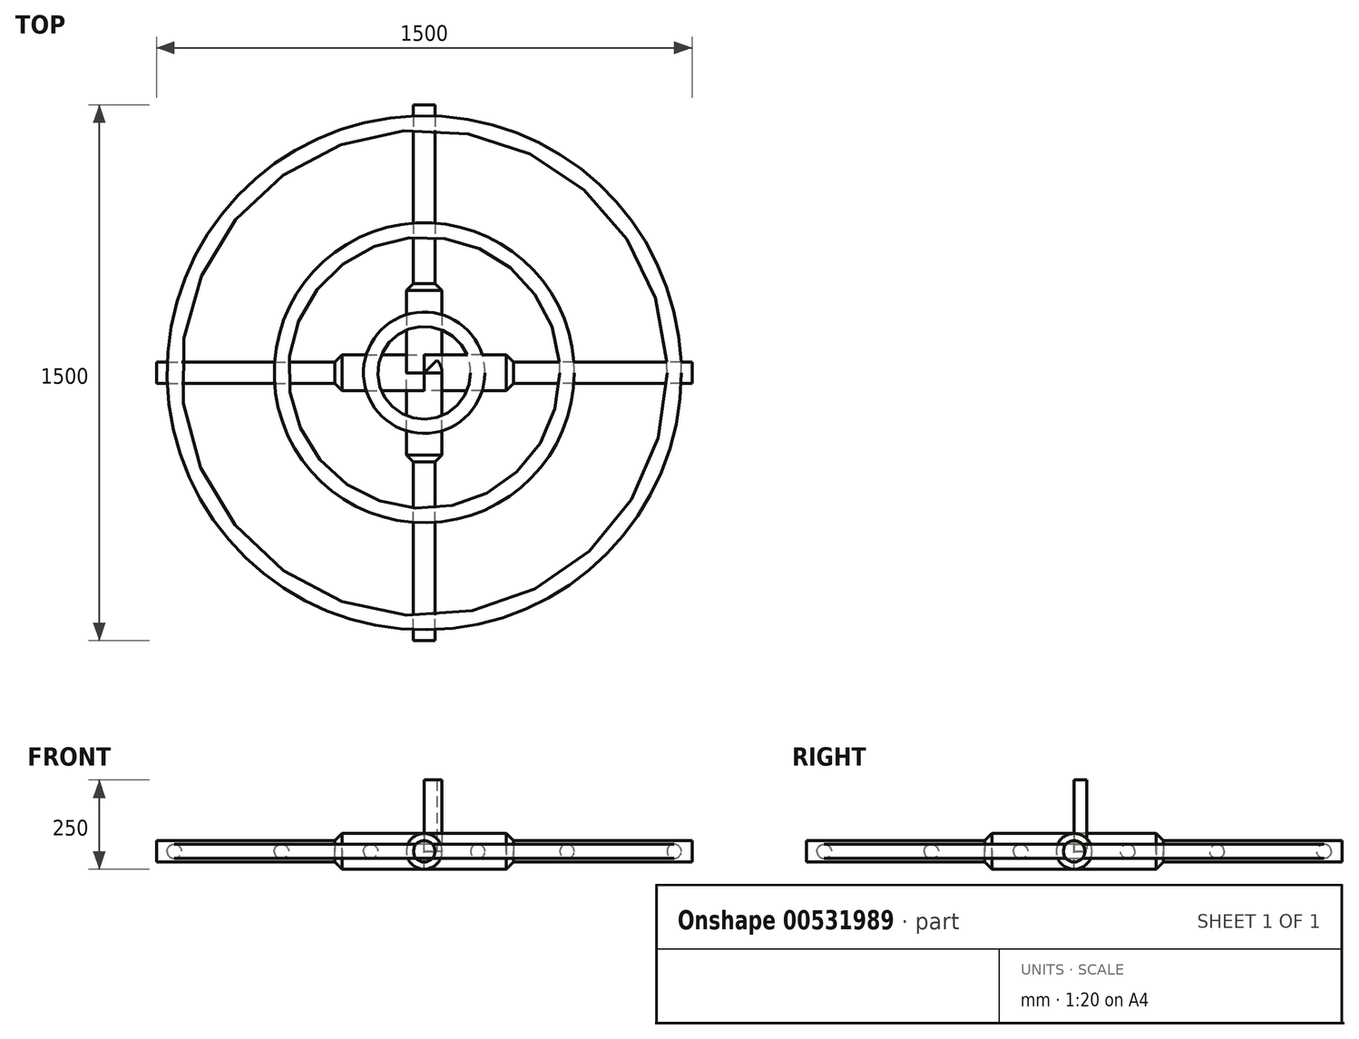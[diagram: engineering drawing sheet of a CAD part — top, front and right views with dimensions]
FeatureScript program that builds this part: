
annotation { "Feature Type Name" : "Feature", "Feature Type Description" : "" }
export const myFeature = defineFeature(function(context is Context, id is Id, definition is map)
    precondition{}
    {
        {
            var Q0;
            Q0=qCreatedBy(makeId("Top.planeOp"),FACE);
            var sketch = newSketch(context, id + "F0", { "sketchPlane" : qUnion([Q0])});
            skCircle(sketch, "E0", {"center": v(0, 0) * mm, "radius": 50 * mm});
            skSolve(sketch);
        }
        {
            var Q0;
            Q0=makeQuery(id+"F0.imprint","IMPRINT",FACE,{"disambiguationData":[TD([[makeQuery(id+"F0.imprint","IMPRINT",EDGE,{"derivedFrom":sQuery(id+"F0.wireOp",EDGE,"E0")}),1.0]])]});
            extrude(context, id + "F1", {"entities" : qUnion([Q0]), "depth" : 200 * mm, "offsetDistance" : 25 * mm});
        }
        {
            var Q0;
            Q0=qCreatedBy(makeId("Front.planeOp"),FACE);
            var sketch = newSketch(context, id + "F2", { "sketchPlane" : qUnion([Q0])});
            skCircle(sketch, "E1", {"center": v(0, 0) * mm, "radius": 50 * mm});
            skSolve(sketch);
        }
        {
            var Q0;
            Q0 = qSketchRegion(id + "F2", true);
            extrude(context, id + "F3", {"entities" : qUnion([Q0]), "depth" : 250 * mm, "offsetDistance" : 25 * mm});
        }
        {
            var Q0;
            Q0=makeQuery(id+"F3.opExtrude","CAP_FACE",FACE,{"disambiguationData":[OSD([sQuery(id+"F2.wireOp",EDGE,"E1")])],"isStart":false});
            var sketch = newSketch(context, id + "F4", { "sketchPlane" : qUnion([Q0])});
            skCircle(sketch, "E2", {"center": v(0, 0) * mm, "radius": 30 * mm});
            skSolve(sketch);
        }
        {
            var Q0;
            Q0=makeQuery(id+"F4.imprint","IMPRINT",FACE,{"disambiguationData":[TD([[makeQuery(id+"F4.imprint","IMPRINT",EDGE,{"derivedFrom":sQuery(id+"F4.wireOp",EDGE,"E2")}),1.0]])]});
            extrude(context, id + "F5", {"entities" : qUnion([Q0]), "operationType" : NewBodyOperationType.ADD, "depth" : 500 * mm, "offsetDistance" : 25 * mm});
        }
        {
            var Q0;
            Q0=makeQuery(id+"F3.opExtrude","CAP_EDGE",EDGE,{"disambiguationData":[OSD([sQuery(id+"F2.wireOp",EDGE,"E1")])],"isStart":false});
            chamfer(context, id + "F6", {"entities" : qUnion([Q0]), "width" : 20 * mm, "tangentPropagation" : true});
        }
        {
            var Q0;
            Q0=qCreatedBy(makeId("Right.planeOp"),FACE);
            var sketch = newSketch(context, id + "F7", { "sketchPlane" : qUnion([Q0])});
            skCircle(sketch, "E3", {"center": v(-150, 0) * mm, "radius": 20 * mm});
            skCircle(sketch, "E4", {"center": v(-400, 0) * mm, "radius": 20 * mm});
            skCircle(sketch, "E5", {"center": v(-700, 0) * mm, "radius": 20 * mm});
            skSolve(sketch);
        }
        {
            var Q0;
            Q0=qCreatedBy(makeId("Top.planeOp"),FACE);
            var sketch = newSketch(context, id + "F8", { "sketchPlane" : qUnion([Q0])});
            skPoint(sketch, "E6", {"position": v(0, 0) * mm});
            skPoint(sketch, "E7.0", {"position": v(0, -150) * mm});
            skPoint(sketch, "E8.0", {"position": v(0, -400) * mm});
            skPoint(sketch, "E9.0", {"position": v(0, -700) * mm});
            skCircle(sketch, "E10", {"center": v(0, 0) * mm, "radius": 150 * mm});
            skCircle(sketch, "E11", {"center": v(0, 0) * mm, "radius": 400 * mm});
            skCircle(sketch, "E12", {"center": v(0, 0) * mm, "radius": 700 * mm});
            skSolve(sketch);
        }
        {
            var Q0;
            Q0=makeQuery(id+"F7.imprint","IMPRINT",FACE,{"disambiguationData":[TD([[makeQuery(id+"F7.imprint","IMPRINT",EDGE,{"derivedFrom":sQuery(id+"F7.wireOp",EDGE,"E3")}),1.0]])]});
            var Q1;
            Q1=sQuery(id+"F8.wireOp",EDGE,"E10");
            sweep(context, id + "F9", {"profiles" : qUnion([Q0]), "path" : qUnion([Q1])});
        }
        {
            var Q0;
            Q0=makeQuery(id+"F7.imprint","IMPRINT",FACE,{"disambiguationData":[TD([[makeQuery(id+"F7.imprint","IMPRINT",EDGE,{"derivedFrom":sQuery(id+"F7.wireOp",EDGE,"E4")}),1.0]])]});
            var Q1;
            Q1=sQuery(id+"F8.wireOp",EDGE,"E11");
            sweep(context, id + "F10", {"profiles" : qUnion([Q0]), "path" : qUnion([Q1])});
        }
        {
            var Q0;
            Q0=makeQuery(id+"F7.imprint","IMPRINT",FACE,{"disambiguationData":[TD([[makeQuery(id+"F7.imprint","IMPRINT",EDGE,{"derivedFrom":sQuery(id+"F7.wireOp",EDGE,"E5")}),1.0]])]});
            var Q1;
            Q1=sQuery(id+"F8.wireOp",EDGE,"E12");
            sweep(context, id + "F11", {"profiles" : qUnion([Q0]), "path" : qUnion([Q1])});
        }
        {
            var Q0;
            Q0=makeQuery(id+"F5.opExtrude","SWEPT_BODY",BODY,{"disambiguationData":[OSD([sQuery(id+"F4.wireOp",EDGE,"E2")])]});
            var Q1;
            Q1=makeQuery(id+"F3.opExtrude","SWEPT_BODY",BODY,{"disambiguationData":[OSD([sQuery(id+"F2.wireOp",EDGE,"E1")])]});
            var Q2;
            Q2=makeQuery(id+"F1.opExtrude","SWEPT_FACE",FACE,{"disambiguationData":[OSD([sQuery(id+"F0.wireOp",EDGE,"E0")])]});
            circularPattern(context, id + "F12", {"entities" : qUnion([Q0, Q1]), "axis" : qUnion([Q2]), "angle" : 360 * degree, "instanceCount" : 4, "equalSpace" : true});
        }
        {
            var Q0;
            Q0=qCreatedBy(makeId("Top.planeOp"),FACE);
            var sketch = newSketch(context, id + "F13", { "sketchPlane" : qUnion([Q0])});
            skArc(sketch, "E13", {"start": v(824.32, 0) * mm, "mid": v(761.57, 315.45) * mm, "end": v(582.88, 582.88) * mm});
            skLineSegment(sketch, "E14", {"start": v(824.32, 0) * mm, "end": v(0, 0) * mm});
            skLineSegment(sketch, "E15", {"start": v(0, 0) * mm, "end": v(582.88, 582.88) * mm});
            skSolve(sketch);
        }
        {
            var Q0;
            Q0=makeQuery(id+"F13.imprint","IMPRINT",FACE,{"disambiguationData":[TD([[makeQuery(id+"F13.imprint","IMPRINT",EDGE,{"derivedFrom":sQuery(id+"F13.wireOp",EDGE,"XqTlJVcp-0IXx-OEdI-8W9Q-iauccixGu5Id.bottom")}),1.0]])]});
            var Q1;
            Q1=makeQuery(id+"F13.imprint","IMPRINT",FACE,{"disambiguationData":[TD([[makeQuery(id+"F13.imprint","IMPRINT",EDGE,{"derivedFrom":sQuery(id+"F13.wireOp",EDGE,"E13")}),1.0]])]});
            extrude(context, id + "F14", {"entities" : qUnion([Q0, Q1]), "endBound" : BoundingType.SYMMETRIC, "depth" : 500 * mm, "offsetDistance" : 25 * mm});
        }
        {
            var Q0;
            Q0=makeQuery(id+"F1.opExtrude","SWEPT_BODY",BODY,{"disambiguationData":[OSD([sQuery(id+"F0.wireOp",EDGE,"E0")])]});
            var Q1;
            Q1=makeQuery(id+"F14.opExtrude","SWEPT_BODY",BODY,{"disambiguationData":[OSD([sQuery(id+"F13.wireOp",EDGE,"E13"),sQuery(id+"F13.wireOp",EDGE,"E14"),sQuery(id+"F13.wireOp",EDGE,"E15")])]});
            booleanBodies(context, id + "F15", {"operationType" : BooleanOperationType.INTERSECTION, "tools" : qUnion([Q0, Q1])});
        }
    });
